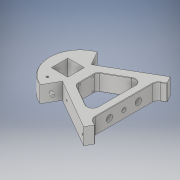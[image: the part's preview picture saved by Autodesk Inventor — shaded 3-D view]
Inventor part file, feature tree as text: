
AUTODESK INVENTOR PART (.ipt)
format: ipt  version: 2019 (Build 230136000, 136)  size: 271,872 bytes
history: native  units: mm
features: sketch x9, extrude x5, fillet x5, hole x4
ambient origin geometry x8: Origin, YZ Plane, XZ Plane, XY Plane, X Axis, Y Axis, Z Axis, Center Point
bodies: Solid1 (feature_tree)
feature tree (23):
  extrude  "Extrusion1"  Depth=40.0mm
  extrude  "Extrusion2"  Depth=20.0mm
  extrude  "Extrusion3"  Depth=40.0mm
  extrude  "Extrusion4"  Depth=40.0mm
  fillet  "Fillet1"  Radius=10.0mm
  fillet  "Fillet2"  Radius=40.0mm
  fillet  "Fillet3"  Radius=40.0mm
  hole  "Hole1"  [1 undecoded]
  hole  "Hole2"  [1 undecoded]
  fillet  "Fillet8"  Radius=25.0mm
  fillet  "Fillet9"  Radius=40.0mm
  hole  "Hole3"  [1 undecoded]
  sketch  "Sketch8"  dims[d28=15.0mm]
  hole  "Hole4"  [1 undecoded]
  extrude  "Extrusion6"  Depth=1.0mm
  sketch  "Sketch1"  dims[d3=40.0mm d4=140.0mm]
  sketch  "Sketch2"  dims[d5=20.0mm d7=20.0mm]
  sketch  "Sketch3"  dims[d8=40.0mm d9=0.0mm d10=6.8mm]
  sketch  "Sketch4"  dims[d11=10.0mm d12=0.0mm d13=6.8mm d14=10.0mm d15=0.0mm d16=40.0mm d17=40.0mm]
  sketch  "Sketch5"  dims[d19=70.0mm d20=75.0mm]
  sketch  "Sketch6"  dims[d21=20.0mm d22=85.0mm d23=25.0mm d24=40.0mm d25=0.0mm]
  sketch  "Sketch7"  dims[d26=10.0mm d27=13.0mm]
  sketch  "Sketch9"  dims[d29=4.0mm d30=6.0mm d31=5.0mm d32=2.0mm d33=14.3117mm d34=4.0mm d35=0.0mm d36=4.0mm d37=6.0mm d38=5.0mm d39=2.0mm d40=14.3117mm d41=4.0mm d42=0.0mm d47=1.0mm d48=1.0mm d49=4.0mm d50=6.0mm d51=5.0mm d52=2.0mm d53=90.0deg d54=8.0mm d55=20.594885mm d56=15.0mm d57=15.0mm d58=20.0mm d59=35.0mm d60=35.0mm d64=19.0mm d67=15.5mm d68=15.5mm d69=15.5mm d70=15.5mm d71=15.5mm d72=15.5mm d73=15.5mm d74=15.5mm d75=4.0mm d76=50.8mm d77=5.0mm d78=2.0mm d79=90.0deg d80=15.0mm d81=20.594885mm d82=10.0mm d83=20.0mm d84=0.0mm]
note: 4 required parameter values undecoded (feature->parameter linkage not recoverable at this tier; creation-order binding heuristic only, values carry confidence <= 0.55)
